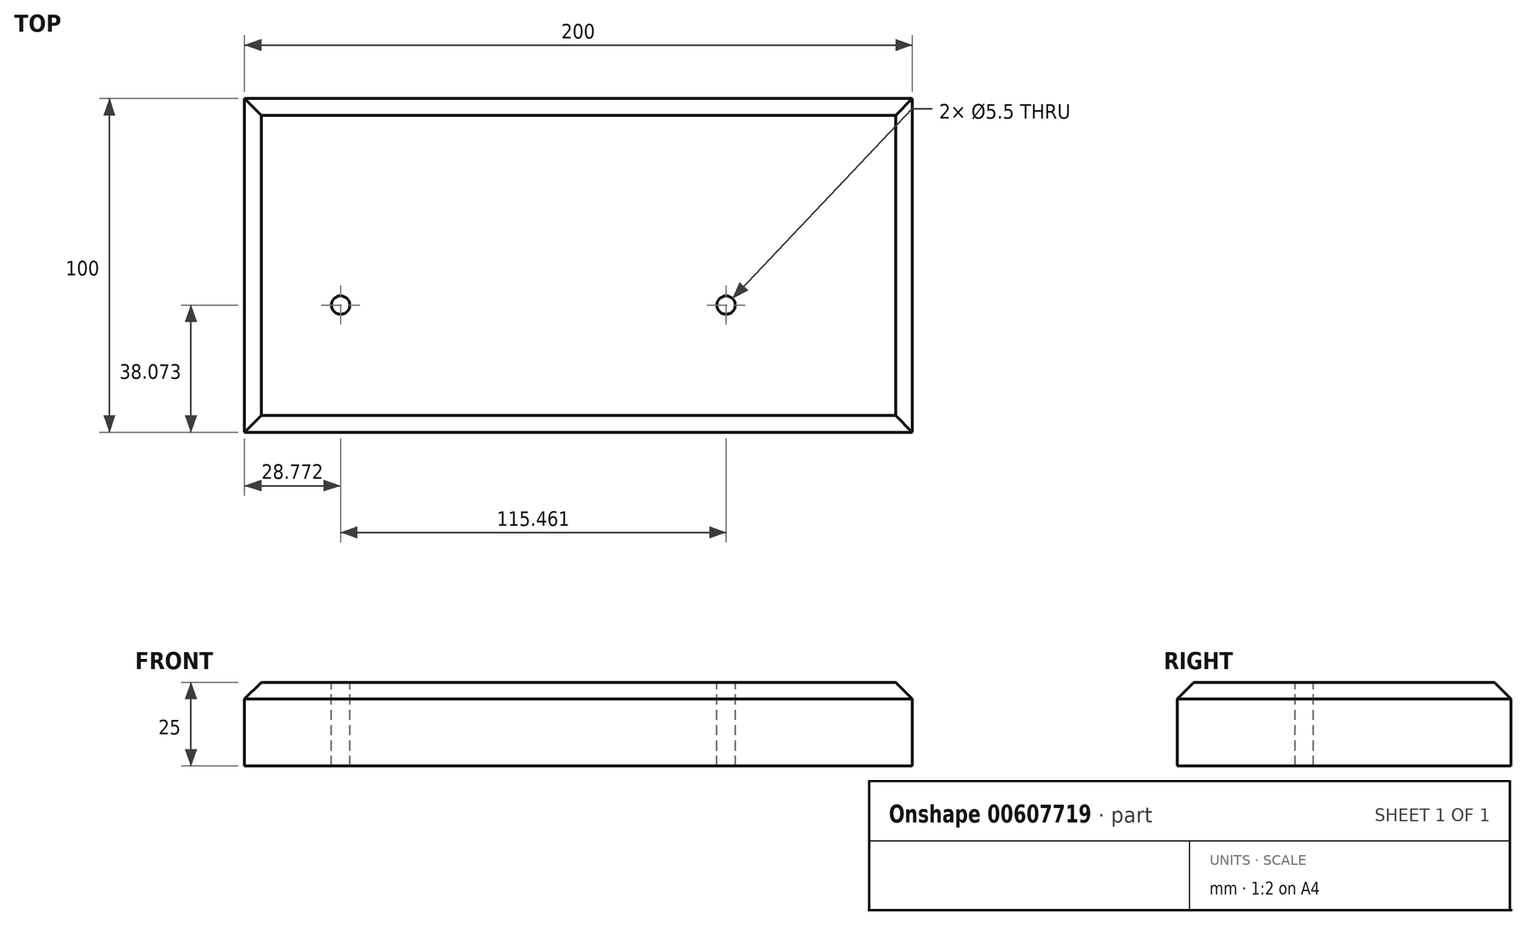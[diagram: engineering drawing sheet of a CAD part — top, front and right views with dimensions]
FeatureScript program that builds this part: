
annotation { "Feature Type Name" : "Feature", "Feature Type Description" : "" }
export const myFeature = defineFeature(function(context is Context, id is Id, definition is map)
    precondition{}
    {
        {
            var Q0;
            Q0=qCreatedBy(makeId("Top.planeOp"),FACE);
            var sketch = newSketch(context, id + "F0", { "sketchPlane" : qUnion([Q0])});
            skLineSegment(sketch, "E0.bottom", {"start": v(-100, 50) * mm, "end": v(100, 50) * mm});
            skLineSegment(sketch, "E0.top", {"start": v(-100, -50) * mm, "end": v(100, -50) * mm});
            skLineSegment(sketch, "E0.left", {"start": v(-100, 50) * mm, "end": v(-100, -50) * mm});
            skLineSegment(sketch, "E0.right", {"start": v(100, 50) * mm, "end": v(100, -50) * mm});
            skPoint(sketch, "E0.middle", {"position": v(0, 0) * mm});
            skSolve(sketch);
        }
        {
            var Q0;
            Q0 = qSketchRegion(id + "F0", true);
            extrude(context, id + "F1", {"entities" : qUnion([Q0]), "depth" : 25 * mm, "offsetDistance" : 25 * mm});
        }
        {
            var Q0;
            Q0=makeQuery(id+"F1.opExtrude","CAP_FACE",FACE,{"disambiguationData":[OSD([sQuery(id+"F0.wireOp",EDGE,"E0.bottom"),sQuery(id+"F0.wireOp",EDGE,"E0.top"),sQuery(id+"F0.wireOp",EDGE,"E0.left"),sQuery(id+"F0.wireOp",EDGE,"E0.right")])],"isStart":false});
            var sketch = newSketch(context, id + "F2", { "sketchPlane" : qUnion([Q0])});
            skPoint(sketch, "E1", {"position": v(-71.23, -11.93) * mm});
            skPoint(sketch, "E2", {"position": v(44.23, -11.93) * mm});
            skSolve(sketch);
        }
        {
            var Q0;
            Q0=sQuery(id+"F2.wireOp",VERTEX,"E1");
            var Q1;
            Q1=sQuery(id+"F2.wireOp",VERTEX,"E2");
            var Q2;
            Q2=makeQuery(id+"F1.opExtrude","SWEPT_BODY",BODY,{"disambiguationData":[OSD([sQuery(id+"F0.wireOp",EDGE,"E0.bottom"),sQuery(id+"F0.wireOp",EDGE,"E0.top"),sQuery(id+"F0.wireOp",EDGE,"E0.left"),sQuery(id+"F0.wireOp",EDGE,"E0.right")])]});
            hole(context, id + "F3", {"style" : HoleStyle.SIMPLE, "endStyle" : HoleEndStyle.THROUGH, "standardTappedOrClearance" : lookupTablePath({ "standard" : "ISO", "fit" : "Normal", "size" : "M5", "type" : "Clearance" }), "standardBlindInLast" : lookupTablePath({ "fit" : "Standard", "standard" : "ISO", "size" : "M5", "type" : "Clearance" }), "holeDiameter" : 5.5 * mm, "majorDiameter" : 5 * mm, "isTappedThrough" : true, "tappedDepth" : 12 * mm, "tapClearance" : 3, "locations" : qUnion([Q0, Q1]), "scope" : qUnion([Q2])});
        }
        {
            var Q0;
            Q0=makeQuery(id+"F1.opExtrude","CAP_EDGE",EDGE,{"disambiguationData":[OSD([sQuery(id+"F0.wireOp",EDGE,"E0.top")])],"isStart":false});
            var Q1;
            Q1=makeQuery(id+"F1.opExtrude","CAP_EDGE",EDGE,{"disambiguationData":[OSD([sQuery(id+"F0.wireOp",EDGE,"E0.left")])],"isStart":false});
            var Q2;
            Q2=makeQuery(id+"F1.opExtrude","CAP_EDGE",EDGE,{"disambiguationData":[OSD([sQuery(id+"F0.wireOp",EDGE,"E0.bottom")])],"isStart":false});
            var Q3;
            Q3=makeQuery(id+"F1.opExtrude","CAP_EDGE",EDGE,{"disambiguationData":[OSD([sQuery(id+"F0.wireOp",EDGE,"E0.right")])],"isStart":false});
            chamfer(context, id + "F4", {"entities" : qUnion([Q0, Q1, Q2, Q3]), "width" : 5 * mm, "tangentPropagation" : true});
        }
    });
